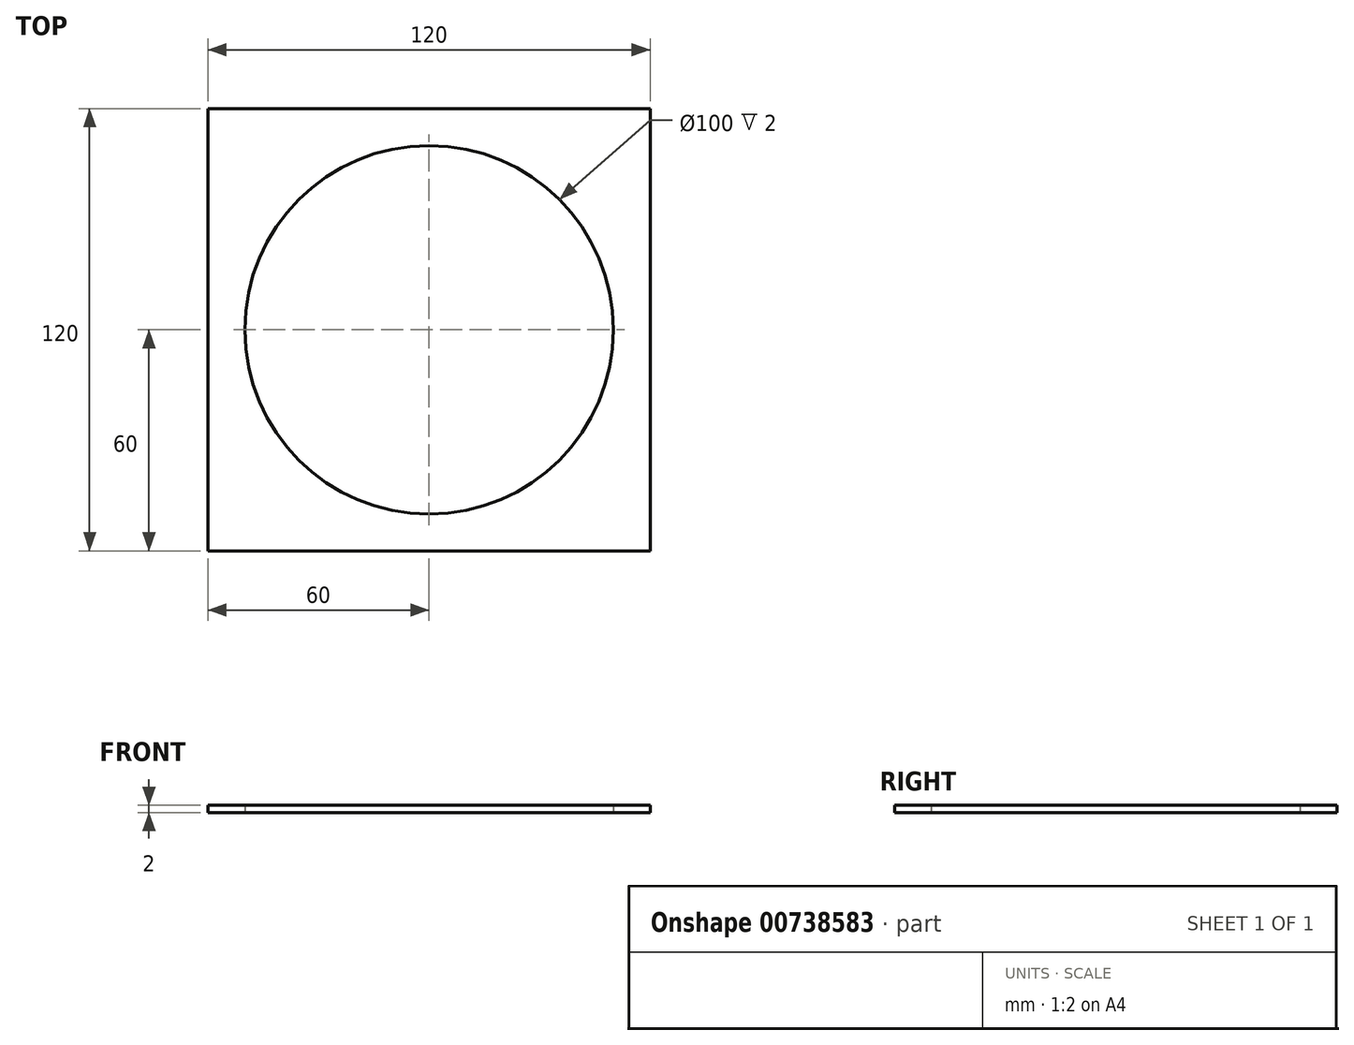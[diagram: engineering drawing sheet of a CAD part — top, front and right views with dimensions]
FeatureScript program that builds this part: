
annotation { "Feature Type Name" : "Feature", "Feature Type Description" : "" }
export const myFeature = defineFeature(function(context is Context, id is Id, definition is map)
    precondition{}
    {
        {
            var Q0;
            Q0=qCreatedBy(makeId("Top.planeOp"),FACE);
            var sketch = newSketch(context, id + "F0", { "sketchPlane" : qUnion([Q0])});
            skLineSegment(sketch, "E0.bottom", {"start": v(-60, 60) * mm, "end": v(60, 60) * mm});
            skLineSegment(sketch, "E0.top", {"start": v(-60, -60) * mm, "end": v(60, -60) * mm});
            skLineSegment(sketch, "E0.left", {"start": v(-60, 60) * mm, "end": v(-60, -60) * mm});
            skLineSegment(sketch, "E0.right", {"start": v(60, 60) * mm, "end": v(60, -60) * mm});
            skPoint(sketch, "E0.middle", {"position": v(0, 0) * mm});
            skCircle(sketch, "E1", {"center": v(0, 0) * mm, "radius": 50 * mm});
            skSolve(sketch);
        }
        {
            var Q0;
            Q0=makeQuery(id+"F0.imprint","IMPRINT",FACE,{"disambiguationData":[TD([[makeQuery(id+"F0.imprint","IMPRINT",EDGE,{"derivedFrom":sQuery(id+"F0.wireOp",EDGE,"E0.bottom")}),-1.0]])]});
            extrude(context, id + "F1", {"entities" : qUnion([Q0]), "depth" : 2 * mm, "offsetDistance" : 25 * mm});
        }
    });
